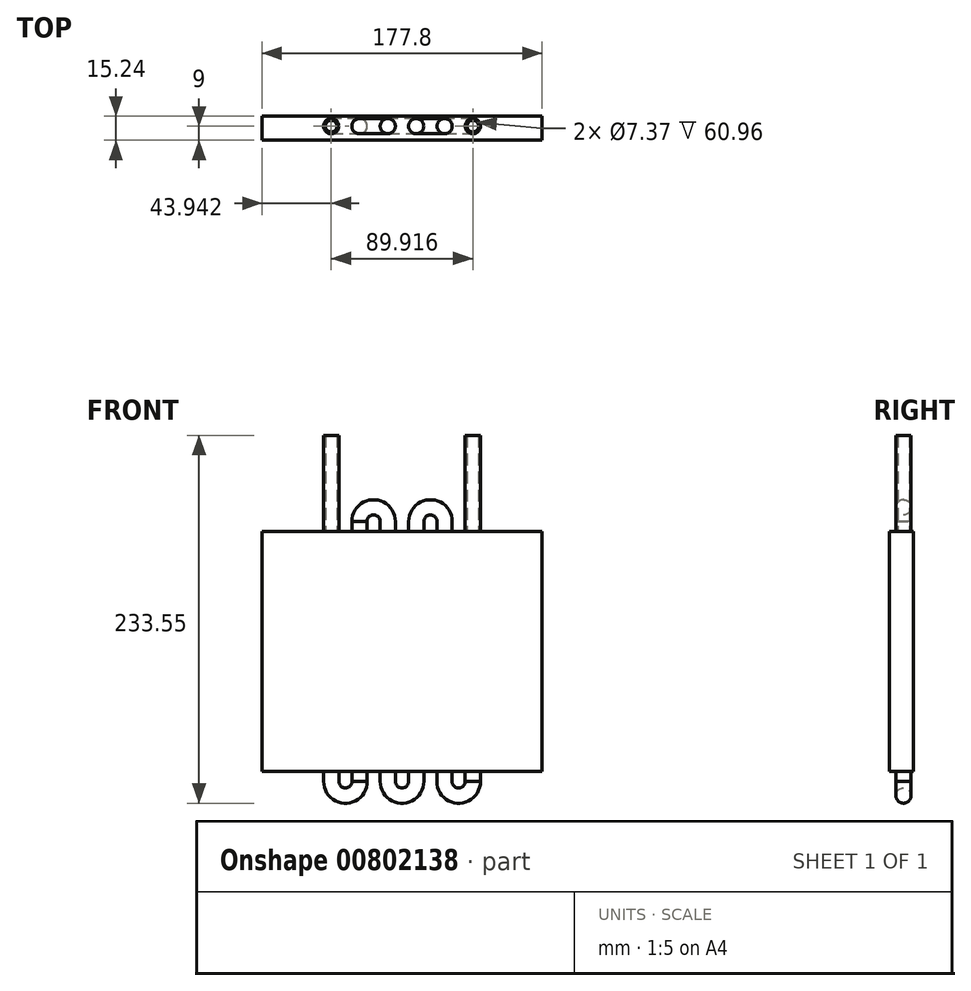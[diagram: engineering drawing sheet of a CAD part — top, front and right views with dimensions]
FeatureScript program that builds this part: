
annotation { "Feature Type Name" : "Feature", "Feature Type Description" : "" }
export const myFeature = defineFeature(function(context is Context, id is Id, definition is map)
    precondition{}
    {
        {
            var Q0;
            Q0=qCreatedBy(makeId("Front.planeOp"),FACE);
            var sketch = newSketch(context, id + "F0", { "sketchPlane" : qUnion([Q0])});
            skLineSegment(sketch, "E0.bottom", {"start": v(0, 0) * mm, "end": v(-177.8, 0) * mm});
            skLineSegment(sketch, "E0.top", {"start": v(0, 152.4) * mm, "end": v(-177.8, 152.4) * mm});
            skLineSegment(sketch, "E0.left", {"start": v(0, 0) * mm, "end": v(0, 152.4) * mm});
            skLineSegment(sketch, "E0.right", {"start": v(-177.8, 0) * mm, "end": v(-177.8, 152.4) * mm});
            skSolve(sketch);
        }
        {
            var Q0;
            Q0=qSketchRegion(id+"F0",true);
            extrude(context, id + "F1", {"entities" : qUnion([Q0]), "depth" : 15.24 * mm});
        }
        {
            var Q0;
            Q0=makeQuery(id+"F1.opExtrude","SWEPT_FACE",FACE,{"disambiguationData":[OSD([sQuery(id+"F0.wireOp",EDGE,"E0.top")])]});
            var sketch = newSketch(context, id + "F2", { "sketchPlane" : qUnion([Q0])});
            skCircle(sketch, "E1", {"center": v(-133.86, -6.24) * mm, "radius": 4.83 * mm});
            skCircle(sketch, "E2", {"center": v(-43.94, -6.24) * mm, "radius": 4.83 * mm});
            skCircle(sketch, "E3", {"center": v(-133.86, -6.24) * mm, "radius": 3.68 * mm});
            skCircle(sketch, "E4", {"center": v(-43.94, -6.24) * mm, "radius": 3.68 * mm});
            skSolve(sketch);
        }
        {
            var Q0;
            Q0=qSketchRegion(id+"F2",true);
            extrude(context, id + "F3", {"entities" : qUnion([Q0]), "operationType" : NewBodyOperationType.ADD, "depth" : 60.96 * mm});
        }
        {
            var Q0;
            {var subQ2=sQuery(id+"F0.wireOp",EDGE,"E0.left");var subQ3=sQuery(id+"F0.wireOp",EDGE,"E0.top");Q0=makeQuery(id+"F3.boolean.opBoolean","SPLIT",FACE,{"disambiguationData":[TD([makeQuery(id+"F1.opExtrude","SWEPT_FACE",FACE,{"disambiguationData":[OSD([subQ2])]})])],"derivedFrom":makeQuery(id+"F1.opExtrude","SWEPT_FACE",FACE,{"disambiguationData":[OSD([subQ3])]})});}
            var sketch = newSketch(context, id + "F4", { "sketchPlane" : qUnion([Q0])});
            skLineSegment(sketch, "E5", {"start": v(-88.9, 0) * mm, "end": v(-88.9, -15.24) * mm, "construction": true});
            skLineSegment(sketch, "E6", {"start": v(-133.86, -6.24) * mm, "end": v(-43.94, -6.24) * mm, "construction": true});
            skCircle(sketch, "E7", {"center": v(-97.92, -6.24) * mm, "radius": 4.83 * mm});
            skCircle(sketch, "E8", {"center": v(-79.88, -6.24) * mm, "radius": 4.83 * mm});
            skCircle(sketch, "E9", {"center": v(-115.95, -6.24) * mm, "radius": 4.83 * mm});
            skCircle(sketch, "E10", {"center": v(-61.85, -6.24) * mm, "radius": 4.83 * mm});
            skSolve(sketch);
        }
        {
            var Q0;
            Q0=qSketchRegion(id+"F4",true);
            extrude(context, id + "F5", {"entities" : qUnion([Q0]), "operationType" : NewBodyOperationType.ADD, "depth" : 6.35 * mm});
        }
        {
            var Q0;
            Q0=makeQuery(id+"F5.opExtrude","CAP_FACE",FACE,{"disambiguationData":[OSD([sQuery(id+"F4.wireOp",EDGE,"E7")])],"isStart":false});
            var sketch = newSketch(context, id + "F6", { "sketchPlane" : qUnion([Q0])});
            skCircle(sketch, "E11", {"center": v(-79.88, -6.24) * mm, "radius": 4.83 * mm});
            skLineSegment(sketch, "E12", {"start": v(-79.88, -6.24) * mm, "end": v(-61.85, -6.24) * mm, "construction": true});
            skLineSegment(sketch, "E13", {"start": v(-97.92, -6.24) * mm, "end": v(-115.95, -6.24) * mm, "construction": true});
            skLineSegment(sketch, "E14", {"start": v(-106.93, -6.24) * mm, "end": v(-106.93, -17.2) * mm, "construction": true});
            skLineSegment(sketch, "E15", {"start": v(-70.87, -6.24) * mm, "end": v(-70.87, -17.31) * mm, "construction": true});
            skSolve(sketch);
        }
        {
            var Q0;
            Q0=makeQuery(id+"F1.opExtrude","SWEPT_FACE",FACE,{"disambiguationData":[OSD([sQuery(id+"F0.wireOp",EDGE,"E0.bottom")])]});
            var sketch = newSketch(context, id + "F7", { "sketchPlane" : qUnion([Q0])});
            skCircle(sketch, "E16", {"center": v(-115.86, 6.24) * mm, "radius": 4.83 * mm});
            skCircle(sketch, "E17", {"center": v(-61.94, 6.24) * mm, "radius": 4.83 * mm});
            skCircle(sketch, "E18", {"center": v(-133.86, 6.24) * mm, "radius": 4.83 * mm});
            skCircle(sketch, "E19", {"center": v(-43.94, 6.24) * mm, "radius": 4.83 * mm});
            skCircle(sketch, "E20", {"center": v(-97.92, 6.24) * mm, "radius": 4.83 * mm});
            skCircle(sketch, "E21", {"center": v(-79.88, 6.24) * mm, "radius": 4.83 * mm});
            skSolve(sketch);
        }
        {
            var Q0;
            Q0=qSketchRegion(id+"F6",true);
            var Q1;
            Q1=sQuery(id+"F6.wireOp",EDGE,"E15");
            revolve(context, id + "F8", {"operationType" : NewBodyOperationType.ADD, "entities" : qUnion([Q0]), "axis" : qUnion([Q1]), "revolveType" : RevolveType.ONE_DIRECTION, "oppositeDirection" : true, "angle" : 180 * degree});
        }
        {
            var Q0;
            Q0=makeQuery(id+"F5.opExtrude","CAP_FACE",FACE,{"disambiguationData":[OSD([sQuery(id+"F4.wireOp",EDGE,"E7")])],"isStart":false});
            var sketch = newSketch(context, id + "F9", { "sketchPlane" : qUnion([Q0])});
            skCircle(sketch, "E22", {"center": v(-97.92, -6.24) * mm, "radius": 4.83 * mm});
            skLineSegment(sketch, "E23", {"start": v(-97.92, -6.24) * mm, "end": v(-115.91, -6.24) * mm, "construction": true});
            skLineSegment(sketch, "E24", {"start": v(-106.91, -6.24) * mm, "end": v(-106.91, -17.75) * mm, "construction": true});
            skPoint(sketch, "E24.endSnap0", {"position": v(-106.91, -6.24) * mm});
            skSolve(sketch);
        }
        {
            var Q0;
            Q0=qSketchRegion(id+"F9",true);
            var Q1;
            Q1=sQuery(id+"F9.wireOp",EDGE,"E24");
            revolve(context, id + "F10", {"operationType" : NewBodyOperationType.ADD, "entities" : qUnion([Q0]), "axis" : qUnion([Q1]), "revolveType" : RevolveType.ONE_DIRECTION, "angle" : 180 * degree});
        }
        {
            var Q0;
            Q0=qSketchRegion(id+"F7",true);
            extrude(context, id + "F11", {"entities" : qUnion([Q0]), "operationType" : NewBodyOperationType.ADD, "depth" : 6.35 * mm});
        }
        {
            var Q0;
            Q0=makeQuery(id+"F11.opExtrude","CAP_FACE",FACE,{"disambiguationData":[OSD([sQuery(id+"F7.wireOp",EDGE,"E18")])],"isStart":false});
            var sketch = newSketch(context, id + "F12", { "sketchPlane" : qUnion([Q0])});
            skCircle(sketch, "E25", {"center": v(-133.86, 6.24) * mm, "radius": 4.83 * mm});
            skLineSegment(sketch, "E26", {"start": v(-133.86, 6.24) * mm, "end": v(-115.82, 6.24) * mm, "construction": true});
            skLineSegment(sketch, "E27", {"start": v(-124.84, 6.24) * mm, "end": v(-124.84, 17.31) * mm, "construction": true});
            skSolve(sketch);
        }
        {
            var Q0;
            Q0=qSketchRegion(id+"F12",true);
            var Q1;
            Q1=sQuery(id+"F12.wireOp",EDGE,"E27");
            revolve(context, id + "F13", {"operationType" : NewBodyOperationType.ADD, "entities" : qUnion([Q0]), "axis" : qUnion([Q1]), "revolveType" : RevolveType.ONE_DIRECTION, "angle" : 180 * degree});
        }
        {
            var Q0;
            Q0=makeQuery(id+"F11.opExtrude","CAP_FACE",FACE,{"disambiguationData":[OSD([sQuery(id+"F7.wireOp",EDGE,"E20")])],"isStart":false});
            var sketch = newSketch(context, id + "F14", { "sketchPlane" : qUnion([Q0])});
            skCircle(sketch, "E28", {"center": v(-97.92, 6.24) * mm, "radius": 4.83 * mm});
            skLineSegment(sketch, "E29", {"start": v(-97.92, 6.24) * mm, "end": v(-79.88, 6.24) * mm, "construction": true});
            skLineSegment(sketch, "E30", {"start": v(-88.9, 6.24) * mm, "end": v(-88.9, 16.88) * mm, "construction": true});
            skSolve(sketch);
        }
        {
            var Q0;
            Q0=qSketchRegion(id+"F14",true);
            var Q1;
            Q1=sQuery(id+"F14.wireOp",EDGE,"E30");
            revolve(context, id + "F15", {"operationType" : NewBodyOperationType.ADD, "entities" : qUnion([Q0]), "axis" : qUnion([Q1]), "revolveType" : RevolveType.ONE_DIRECTION, "angle" : 180 * degree});
        }
        {
            var Q0;
            Q0=makeQuery(id+"F11.opExtrude","CAP_FACE",FACE,{"disambiguationData":[OSD([sQuery(id+"F7.wireOp",EDGE,"E17")])],"isStart":false});
            var sketch = newSketch(context, id + "F16", { "sketchPlane" : qUnion([Q0])});
            skCircle(sketch, "E31", {"center": v(-61.94, 6.24) * mm, "radius": 4.83 * mm});
            skLineSegment(sketch, "E32", {"start": v(-61.94, 6.24) * mm, "end": v(-43.9, 6.24) * mm, "construction": true});
            skLineSegment(sketch, "E33", {"start": v(-52.93, 6.24) * mm, "end": v(-52.93, 16.55) * mm, "construction": true});
            skSolve(sketch);
        }
        {
            var Q0;
            Q0=qSketchRegion(id+"F16",true);
            var Q1;
            Q1=sQuery(id+"F16.wireOp",EDGE,"E33");
            revolve(context, id + "F17", {"operationType" : NewBodyOperationType.ADD, "entities" : qUnion([Q0]), "axis" : qUnion([Q1]), "revolveType" : RevolveType.ONE_DIRECTION, "angle" : 180 * degree});
        }
    });
